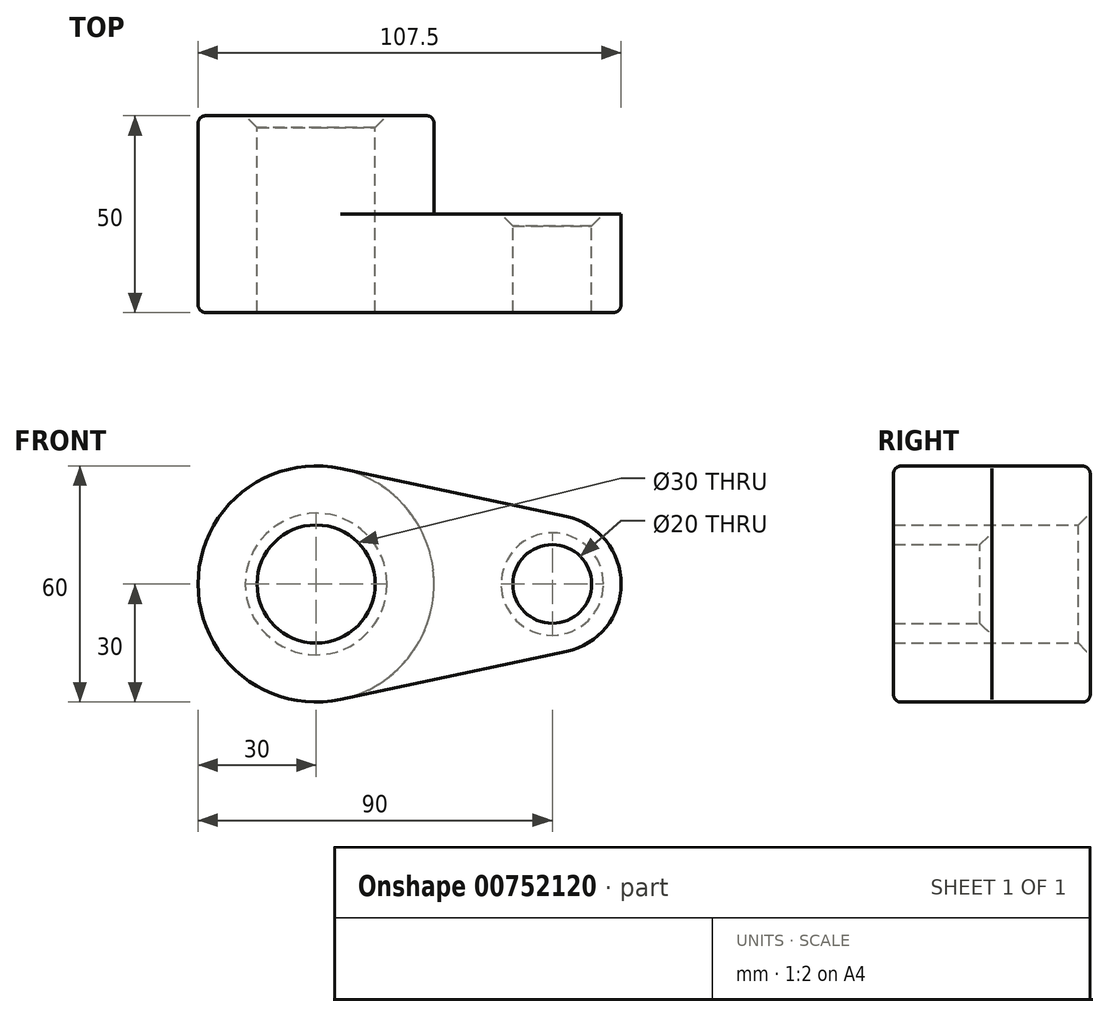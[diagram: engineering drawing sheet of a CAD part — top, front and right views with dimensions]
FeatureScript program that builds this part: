
annotation { "Feature Type Name" : "Feature", "Feature Type Description" : "" }
export const myFeature = defineFeature(function(context is Context, id is Id, definition is map)
    precondition{}
    {
        {
            var Q0;
            Q0=qCreatedBy(makeId("Front.planeOp"),FACE);
            var sketch = newSketch(context, id + "F0", { "sketchPlane" : qUnion([Q0])});
            skCircle(sketch, "E0", {"center": v(0, 0) * mm, "radius": 30 * mm});
            skCircle(sketch, "E1", {"center": v(60, 0) * mm, "radius": 17.5 * mm});
            skLineSegment(sketch, "E2", {"start": v(6.25, 29.34) * mm, "end": v(63.65, 17.12) * mm});
            skLineSegment(sketch, "E3", {"start": v(6.25, -29.34) * mm, "end": v(63.65, -17.12) * mm});
            skCircle(sketch, "E4", {"center": v(0, 0) * mm, "radius": 15 * mm});
            skCircle(sketch, "E5", {"center": v(60, 0) * mm, "radius": 10 * mm});
            skSolve(sketch);
        }
        {
            var Q0;
            Q0=makeQuery(id+"F0.imprint","IMPRINT",FACE,{"disambiguationData":[TD([[makeQuery(id+"F0.imprint","IMPRINT",EDGE,{"derivedFrom":sQuery(id+"F0.wireOp",EDGE,"E4")}),-1.0]])]});
            var Q1;
            {var subQ0=sQuery(id+"F0.wireOp",EDGE,"E2");Q1=makeQuery(id+"F0.imprint","IMPRINT",FACE,{"disambiguationData":[TD([[makeQuery(id+"F0.imprint","IMPRINT",EDGE,{"derivedFrom":subQ0}),-1.0]])]});}
            var Q2;
            Q2=makeQuery(id+"F0.imprint","IMPRINT",FACE,{"disambiguationData":[TD([[makeQuery(id+"F0.imprint","IMPRINT",EDGE,{"derivedFrom":sQuery(id+"F0.wireOp",EDGE,"E5")}),-1.0]])]});
            extrude(context, id + "F1", {"entities" : qUnion([Q0, Q1, Q2]), "depth" : 25 * mm, "offsetDistance" : 25 * mm});
        }
        {
            var Q0;
            Q0=makeQuery(id+"F0.imprint","IMPRINT",FACE,{"disambiguationData":[TD([[makeQuery(id+"F0.imprint","IMPRINT",EDGE,{"derivedFrom":sQuery(id+"F0.wireOp",EDGE,"E4")}),-1.0]])]});
            extrude(context, id + "F2", {"entities" : qUnion([Q0]), "operationType" : NewBodyOperationType.ADD, "oppositeDirection" : true, "depth" : 25 * mm, "offsetDistance" : 25 * mm});
        }
        {
            var Q0;
            Q0=makeQuery(id+"F2.opExtrude","CAP_EDGE",EDGE,{"disambiguationData":[OSD([sQuery(id+"F0.wireOp",EDGE,"E0")])],"isStart":false});
            var Q1;
            Q1=makeQuery(id+"F1.opExtrude","CAP_EDGE",EDGE,{"disambiguationData":[OSD([sQuery(id+"F0.wireOp",EDGE,"E2")])],"isStart":false});
            fillet(context, id + "F3", {"entities" : qUnion([Q0, Q1]), "radius" : 2 * mm, "tangentPropagation" : true, "allowEdgeOverflow" : false});
        }
        {
            var Q0;
            Q0=makeQuery(id+"F2.opExtrude","CAP_EDGE",EDGE,{"disambiguationData":[OSD([sQuery(id+"F0.wireOp",EDGE,"E4")])],"isStart":false});
            var Q1;
            Q1=makeQuery(id+"F1.opExtrude","CAP_EDGE",EDGE,{"disambiguationData":[OSD([sQuery(id+"F0.wireOp",EDGE,"E5")])],"isStart":true});
            chamfer(context, id + "F4", {"entities" : qUnion([Q0, Q1]), "width" : 3 * mm, "tangentPropagation" : true});
        }
    });
